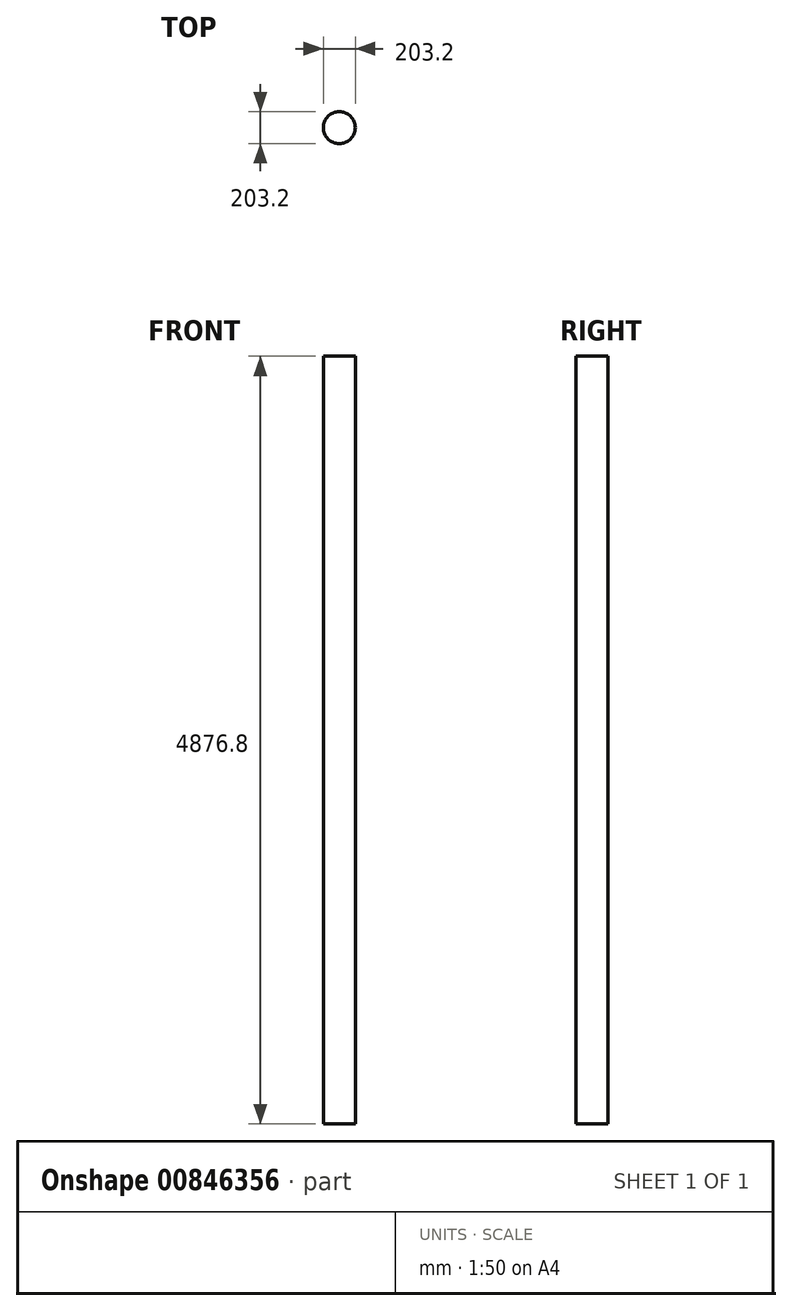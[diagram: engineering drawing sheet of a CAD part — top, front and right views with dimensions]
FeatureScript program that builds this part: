
annotation { "Feature Type Name" : "Feature", "Feature Type Description" : "" }
export const myFeature = defineFeature(function(context is Context, id is Id, definition is map)
    precondition{}
    {
        {
            var Q0;
            Q0=qCreatedBy(makeId("Top.planeOp"),FACE);
            var sketch = newSketch(context, id + "F0", { "sketchPlane" : qUnion([Q0])});
            skCircle(sketch, "E0", {"center": v(0, 0) * mm, "radius": 101.6 * mm});
            skSolve(sketch);
        }
        {
            var Q0;
            Q0 = qSketchRegion(id + "F0", true);
            extrude(context, id + "F1", {"entities" : qUnion([Q0]), "depth" : 4876.8 * mm, "offsetDistance" : 25 * mm});
        }
        {
            var Q0;
            Q0=makeQuery(id+"F1.opExtrude","CAP_FACE",FACE,{"disambiguationData":[OSD([sQuery(id+"F0.wireOp",EDGE,"E0")])],"isStart":false});
            cPlane(context, id + "F2", {"entities" : qUnion([Q0]), "cplaneType" : CPlaneType.OFFSET, "offset" : 609.6 * mm, "oppositeDirection" : true, "width" : 150 * mm, "height" : 150 * mm});
        }
    });
